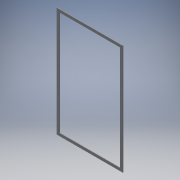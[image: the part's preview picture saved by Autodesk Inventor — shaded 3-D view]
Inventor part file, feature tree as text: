
AUTODESK INVENTOR PART (.ipt)
format: ipt  version: 2017 (Build 210142000, 142)  size: 99,328 bytes
history: native  units: mm
features: extrude x1, sketch x1
ambient origin geometry x8: Origin, YZ Plane, XZ Plane, XY Plane, X Axis, Y Axis, Z Axis, Center Point
bodies: Volumenkörper1 (feature_tree)
feature tree (2):
  extrude  "Extrusion1"  Depth=1200.0mm
  sketch  "Skizze1"  dims[d2=2000.0mm d3=1200.0mm d4=50.0mm d5=10.0mm d6=0.0mm]
